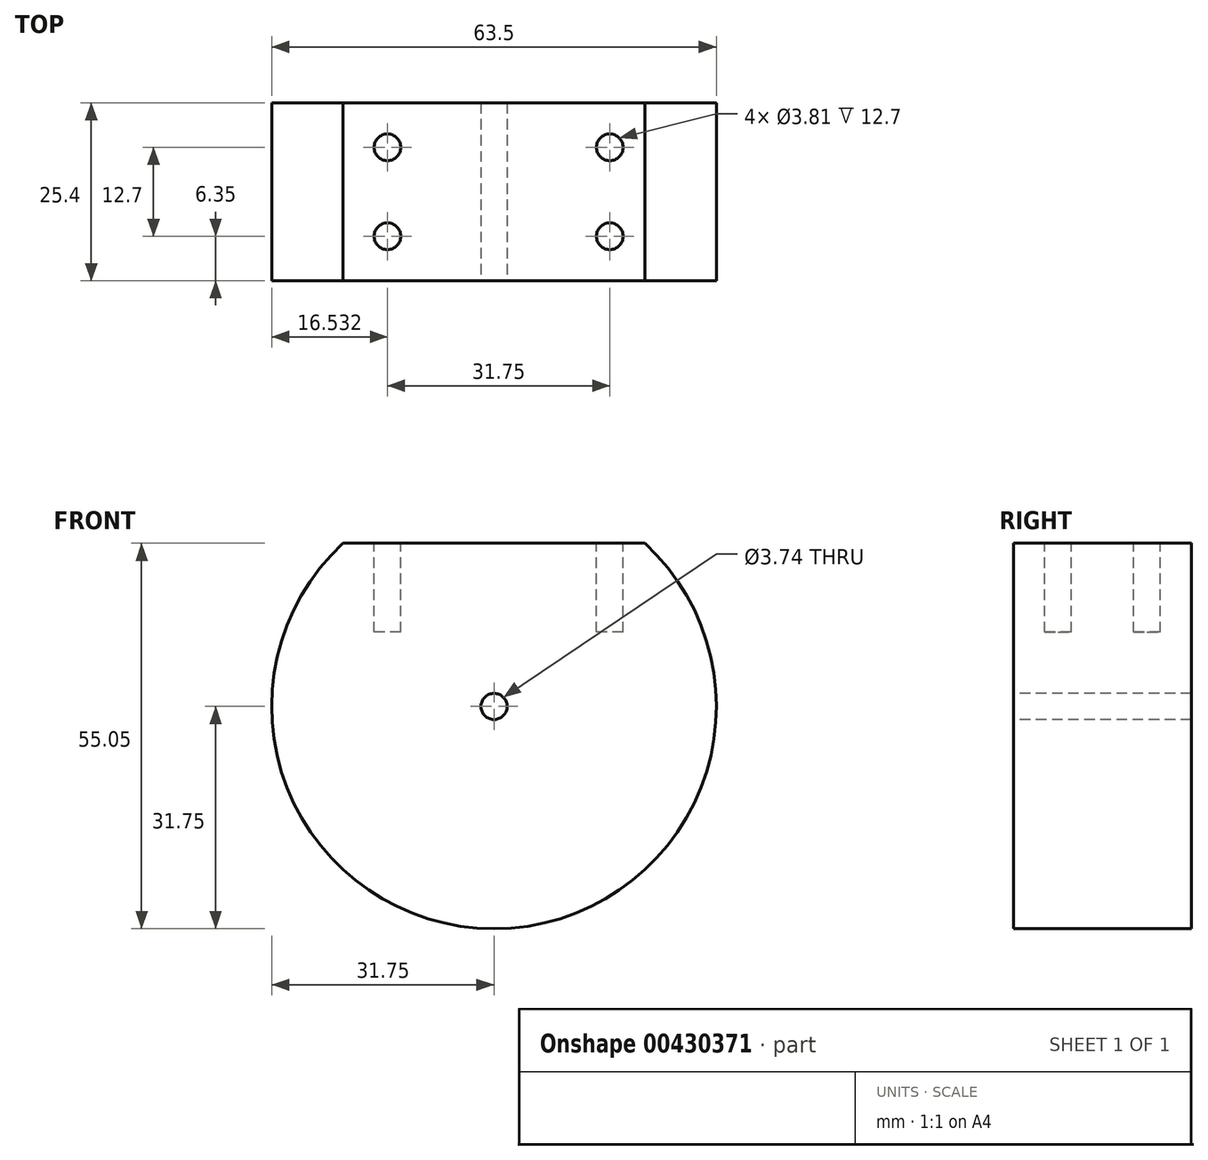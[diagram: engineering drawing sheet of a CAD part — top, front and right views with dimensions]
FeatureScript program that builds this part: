
annotation { "Feature Type Name" : "Feature", "Feature Type Description" : "" }
export const myFeature = defineFeature(function(context is Context, id is Id, definition is map)
    precondition{}
    {
        {
            var Q0;
            Q0=qCreatedBy(makeId("Front.planeOp"),FACE);
            var sketch = newSketch(context, id + "F0", { "sketchPlane" : qUnion([Q0])});
            skCircle(sketch, "E0", {"center": v(0, 0) * mm, "radius": 31.75 * mm});
            skLineSegment(sketch, "E1", {"start": v(-21.57, 23.3) * mm, "end": v(21.57, 23.3) * mm});
            skSolve(sketch);
        }
        {
            var Q0;
            {var subQ0=sQuery(id+"F0.wireOp",EDGE,"E1");Q0=makeQuery(id+"F0.imprint","IMPRINT",FACE,{"disambiguationData":[TD([[makeQuery(id+"F0.imprint","IMPRINT",EDGE,{"derivedFrom":subQ0}),-1.0]])]});}
            extrude(context, id + "F1", {"entities" : qUnion([Q0]), "depth" : 25.4 * mm});
        }
        {
            var Q0;
            Q0=makeQuery(id+"F1.opExtrude","SWEPT_FACE",FACE,{"disambiguationData":[OSD([sQuery(id+"F0.wireOp",EDGE,"E1")])]});
            var sketch = newSketch(context, id + "F2", { "sketchPlane" : qUnion([Q0])});
            skCircle(sketch, "E2", {"center": v(-15.22, -6.35) * mm, "radius": 1.9 * mm});
            skCircle(sketch, "E3.0.1.0", {"center": v(-15.22, -19.05) * mm, "radius": 1.9 * mm});
            skCircle(sketch, "E3.1.0.0", {"center": v(16.53, -6.35) * mm, "radius": 1.9 * mm});
            skCircle(sketch, "E3.1.1.0", {"center": v(16.53, -19.05) * mm, "radius": 1.9 * mm});
            skLineSegment(sketch, "E3.direction1", {"start": v(-15.22, -6.35) * mm, "end": v(16.53, -6.35) * mm, "construction": true});
            skLineSegment(sketch, "E3.direction2", {"start": v(-15.22, -6.35) * mm, "end": v(-15.22, -19.05) * mm, "construction": true});
            skSolve(sketch);
        }
        {
            var Q0;
            Q0=makeQuery(id+"F2.imprint","IMPRINT",FACE,{"disambiguationData":[TD([[makeQuery(id+"F2.imprint","IMPRINT",EDGE,{"derivedFrom":sQuery(id+"F2.wireOp",EDGE,"E2")}),1.0]])]});
            var Q1;
            Q1=makeQuery(id+"F2.imprint","IMPRINT",FACE,{"disambiguationData":[TD([[makeQuery(id+"F2.imprint","IMPRINT",EDGE,{"derivedFrom":sQuery(id+"F2.wireOp",EDGE,"E3.0.1.0")}),1.0]])]});
            var Q2;
            Q2=makeQuery(id+"F2.imprint","IMPRINT",FACE,{"disambiguationData":[TD([[makeQuery(id+"F2.imprint","IMPRINT",EDGE,{"derivedFrom":sQuery(id+"F2.wireOp",EDGE,"E3.1.1.0")}),1.0]])]});
            var Q3;
            Q3=makeQuery(id+"F2.imprint","IMPRINT",FACE,{"disambiguationData":[TD([[makeQuery(id+"F2.imprint","IMPRINT",EDGE,{"derivedFrom":sQuery(id+"F2.wireOp",EDGE,"E3.1.0.0")}),1.0]])]});
            extrude(context, id + "F3", {"entities" : qUnion([Q0, Q1, Q2, Q3]), "operationType" : NewBodyOperationType.REMOVE, "oppositeDirection" : true, "depth" : 12.7 * mm});
        }
        {
            var Q0;
            Q0=makeQuery(id+"F1.opExtrude","CAP_FACE",FACE,{"disambiguationData":[OSD([sQuery(id+"F0.wireOp",EDGE,"E0"),sQuery(id+"F0.wireOp",EDGE,"E1")])],"isStart":false});
            var sketch = newSketch(context, id + "F4", { "sketchPlane" : qUnion([Q0])});
            skCircle(sketch, "E4", {"center": v(0, 0) * mm, "radius": 1.87 * mm});
            skSolve(sketch);
        }
        {
            var Q0;
            Q0=makeQuery(id+"F4.imprint","IMPRINT",FACE,{"disambiguationData":[TD([[makeQuery(id+"F4.imprint","IMPRINT",EDGE,{"derivedFrom":sQuery(id+"F4.wireOp",EDGE,"E4")}),1.0]])]});
            extrude(context, id + "F5", {"entities" : qUnion([Q0]), "operationType" : NewBodyOperationType.REMOVE, "oppositeDirection" : true, "depth" : 25.4 * mm});
        }
    });
